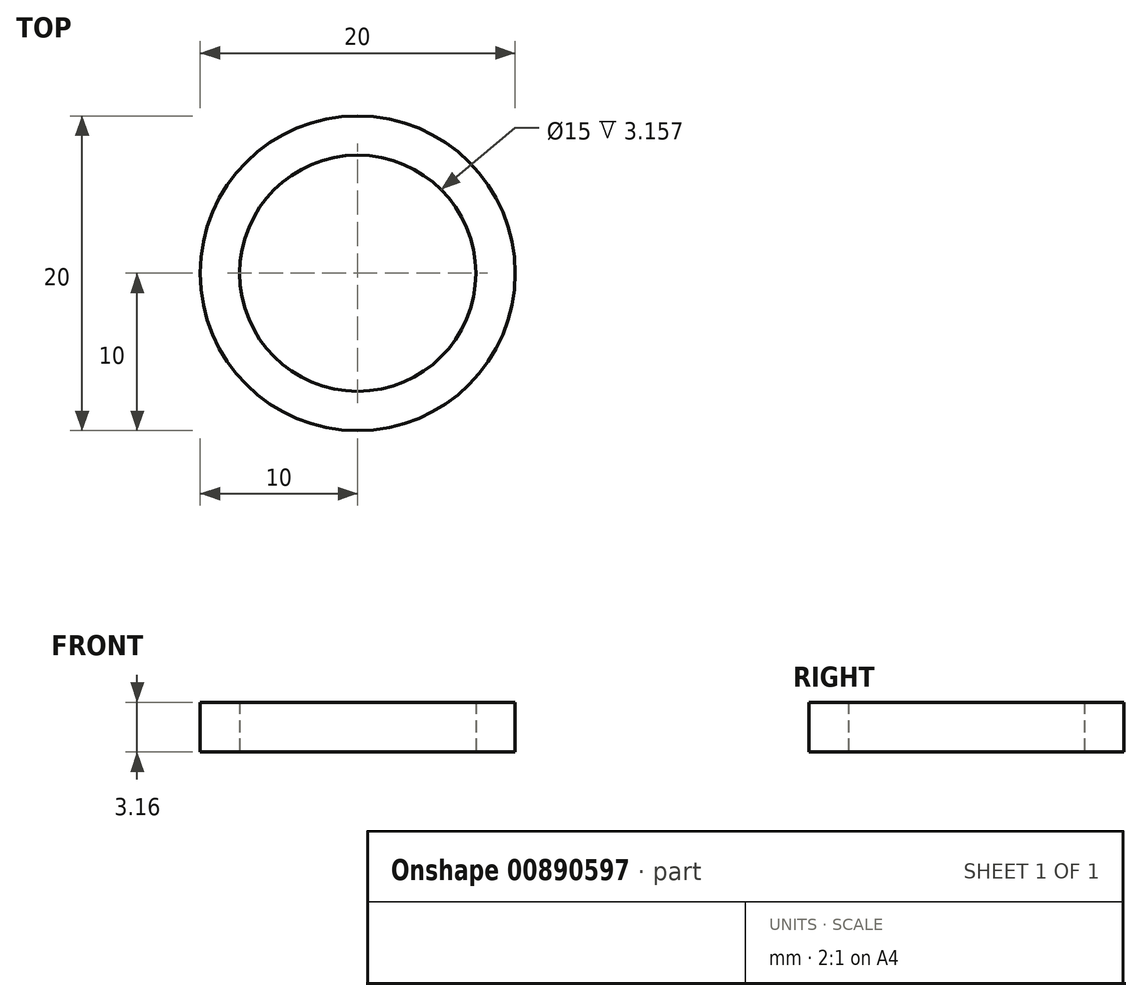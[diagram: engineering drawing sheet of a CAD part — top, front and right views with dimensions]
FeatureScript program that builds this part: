
annotation { "Feature Type Name" : "Feature", "Feature Type Description" : "" }
export const myFeature = defineFeature(function(context is Context, id is Id, definition is map)
    precondition{}
    {
        {
            var Q0;
            Q0=qCreatedBy(makeId("Top.planeOp"),FACE);
            var sketch = newSketch(context, id + "F0", { "sketchPlane" : qUnion([Q0])});
            skCircle(sketch, "E0", {"center": v(0, 0) * mm, "radius": 10 * mm});
            skCircle(sketch, "E1", {"center": v(0, 0) * mm, "radius": 7.5 * mm});
            skSolve(sketch);
        }
        {
            var Q0;
            Q0=makeQuery(id+"F0.imprint","IMPRINT",FACE,{"disambiguationData":[TD([[makeQuery(id+"F0.imprint","IMPRINT",EDGE,{"derivedFrom":sQuery(id+"F0.wireOp",EDGE,"E0")}),1.0]])]});
            extrude(context, id + "F1", {"entities" : qUnion([Q0]), "depth" : 3.16 * mm, "offsetDistance" : 25 * mm});
        }
    });
